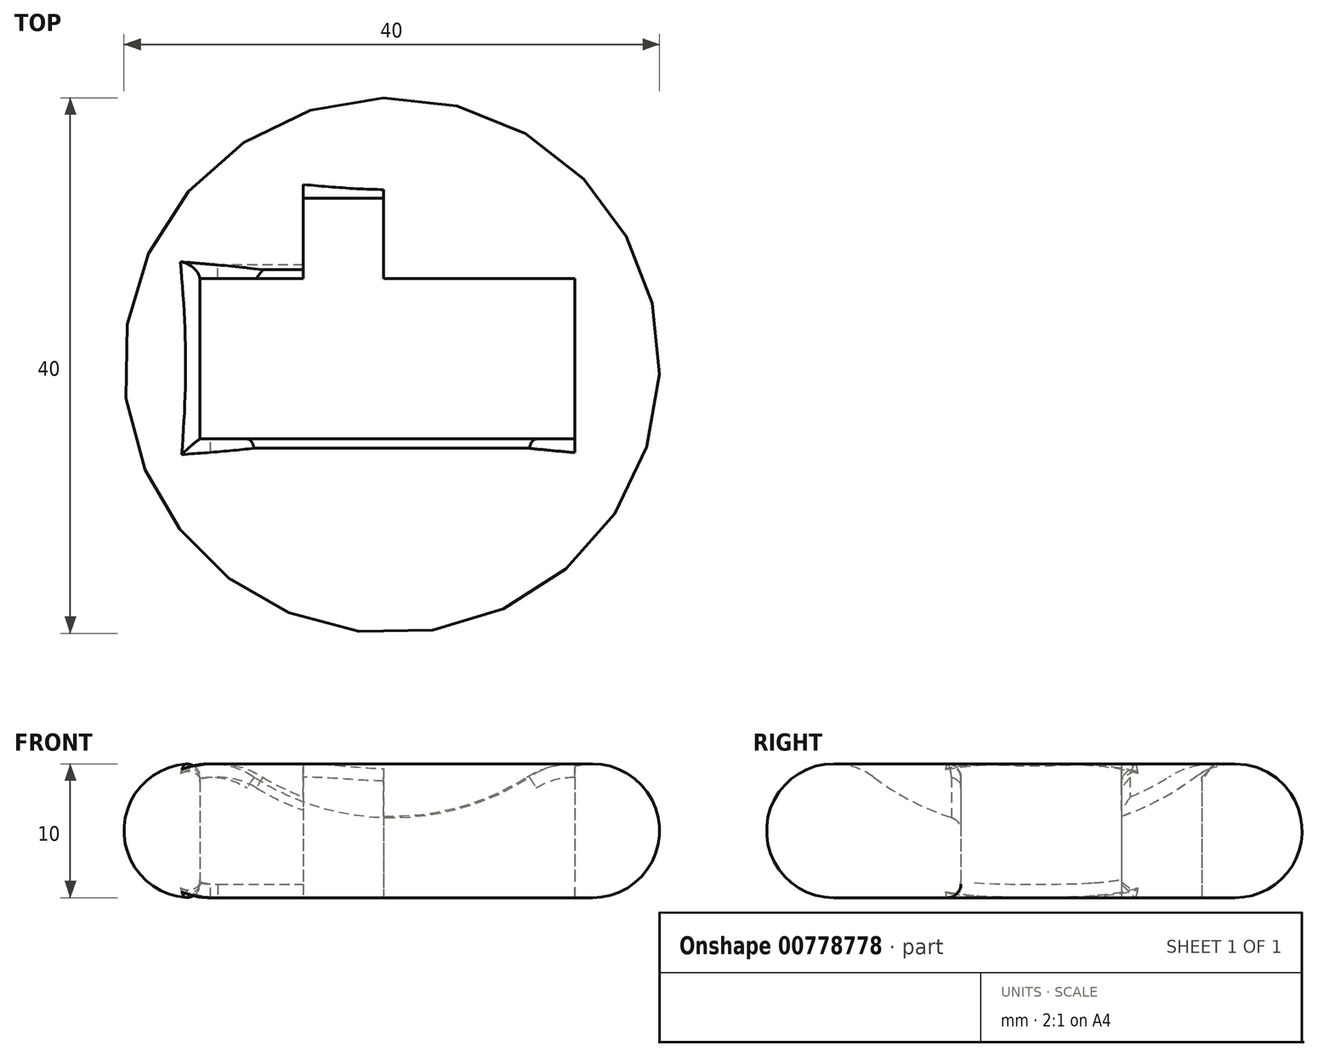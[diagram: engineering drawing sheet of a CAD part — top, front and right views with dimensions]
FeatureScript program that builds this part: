
annotation { "Feature Type Name" : "Feature", "Feature Type Description" : "" }
export const myFeature = defineFeature(function(context is Context, id is Id, definition is map)
    precondition{}
    {
        {
            var Q0;
            Q0=qCreatedBy(makeId("Front.planeOp"),FACE);
            var sketch = newSketch(context, id + "F0", { "sketchPlane" : qUnion([Q0])});
            skArc(sketch, "E0", {"start": v(-12, 9) * mm, "mid": v(-19.74, 6.58) * mm, "end": v(-15, 0) * mm});
            skArc(sketch, "E1", {"start": v(-12, 9) * mm, "mid": v(-6.32, 6.03) * mm, "end": v(0, 5) * mm});
            skLineSegment(sketch, "E2", {"start": v(0, 0) * mm, "end": v(-15, 0) * mm});
            skLineSegment(sketch, "E3", {"start": v(0, 0) * mm, "end": v(0, 5) * mm});
            skSolve(sketch);
        }
        {
            var Q0;
            Q0=makeQuery(id+"F0.imprint","IMPRINT",FACE,{"disambiguationData":[TD([[makeQuery(id+"F0.imprint","IMPRINT",EDGE,{"derivedFrom":sQuery(id+"F0.wireOp",EDGE,"E0")}),1.0]])]});
            var Q1;
            Q1=sQuery(id+"F0.wireOp",EDGE,"E3");
            revolve(context, id + "F1", {"surfaceOperationType" : NewSurfaceOperationType.NEW, "entities" : qUnion([Q0]), "axis" : qUnion([Q1]), "revolveType" : RevolveType.FULL});
        }
        {
            var Q0;
            Q0=qCreatedBy(makeId("Top.planeOp"),FACE);
            var sketch = newSketch(context, id + "F2", { "sketchPlane" : qUnion([Q0])});
            skLineSegment(sketch, "E4.bottom", {"start": v(-14.31, 6.51) * mm, "end": v(13.69, 6.51) * mm});
            skLineSegment(sketch, "E4.top", {"start": v(-14.31, -5.49) * mm, "end": v(13.69, -5.49) * mm});
            skLineSegment(sketch, "E4.left", {"start": v(-14.31, 6.51) * mm, "end": v(-14.31, -5.49) * mm});
            skLineSegment(sketch, "E4.right", {"start": v(13.69, 6.51) * mm, "end": v(13.69, -5.49) * mm});
            skLineSegment(sketch, "E5.bottom", {"start": v(-0.6, 12.51) * mm, "end": v(-6.6, 12.51) * mm});
            skLineSegment(sketch, "E5.top", {"start": v(-0.6, 6.51) * mm, "end": v(-6.6, 6.51) * mm});
            skLineSegment(sketch, "E5.left", {"start": v(-0.6, 12.51) * mm, "end": v(-0.6, 6.51) * mm});
            skLineSegment(sketch, "E5.right", {"start": v(-6.6, 12.51) * mm, "end": v(-6.6, 6.51) * mm});
            skSolve(sketch);
        }
        {
            var Q0;
            Q0 = qSketchRegion(id + "F2", true);
            extrude(context, id + "F3", {"entities" : qUnion([Q0]), "operationType" : NewBodyOperationType.REMOVE, "oppositeDirection" : true, "depth" : -25 * mm, "offsetDistance" : 25 * mm});
        }
        {
            var Q0;
            Q0=makeQuery(id+"F3.boolean.opBoolean","INTERSECT",EDGE,{"disambiguationData":[OD(0.0)],"derivedFrom":[makeQuery(id+"F1.opRevolve","SWEPT_FACE",FACE,{"disambiguationData":[OSD([sQuery(id+"F0.wireOp",EDGE,"E0")])]}),makeQuery(id+"F3.opExtrude","SWEPT_FACE",FACE,{"disambiguationData":[OSD([sQuery(id+"F2.wireOp",EDGE,"E4.left")])]})]});
            fillet(context, id + "F4", {"entities" : qUnion([Q0]), "radius" : 1 * mm, "tangentPropagation" : true, "allowEdgeOverflow" : false});
        }
        {
            var Q0;
            Q0=makeQuery(id+"F3.boolean.opBoolean","INTERSECT",EDGE,{"disambiguationData":[OD(2.0)],"derivedFrom":[makeQuery(id+"F1.opRevolve","SWEPT_FACE",FACE,{"disambiguationData":[OSD([sQuery(id+"F0.wireOp",EDGE,"E0")])]}),makeQuery(id+"F3.opExtrude","SWEPT_FACE",FACE,{"disambiguationData":[OSD([sQuery(id+"F2.wireOp",EDGE,"E4.top")])]})]});
            fillet(context, id + "F5", {"entities" : qUnion([Q0]), "radius" : 1 * mm, "tangentPropagation" : true, "allowEdgeOverflow" : false});
        }
        {
            var Q0;
            Q0=makeQuery(id+"F3.boolean.opBoolean","COPY",EDGE,{"derivedFrom":makeQuery(id+"F3.opExtrude","CAP_EDGE",EDGE,{"disambiguationData":[OSD([sQuery(id+"F2.wireOp",EDGE,"E4.top")])],"isStart":true})});
            var Q1;
            {var subQ0=sQuery(id+"F2.wireOp",EDGE,"E4.bottom");Q1=makeQuery(id+"F3.boolean.opBoolean","INTERSECT",EDGE,{"disambiguationData":[OD(1.0)],"derivedFrom":[makeQuery(id+"F1.opRevolve","SWEPT_FACE",FACE,{"disambiguationData":[OSD([sQuery(id+"F0.wireOp",EDGE,"E0")])]}),makeQuery(id+"F3.opExtrude","SWEPT_FACE",FACE,{"disambiguationData":[OSD([subQ0]),TDD([makeQuery(id+"F2.imprint","IMPRINT",EDGE,{"disambiguationData":[TD([[makeQuery(id+"F2.imprint","INTERSECT",VERTEX,{"derivedFrom":[subQ0,sQuery(id+"F2.wireOp",EDGE,"E4.left")]}),-1.0]])],"derivedFrom":subQ0})])]})]});}
            var Q2;
            Q2=makeQuery(id+"F3.boolean.opBoolean","INTERSECT",EDGE,{"derivedFrom":[makeQuery(id+"F1.opRevolve","SWEPT_FACE",FACE,{"disambiguationData":[OSD([sQuery(id+"F0.wireOp",EDGE,"E0")])]}),makeQuery(id+"F3.opExtrude","SWEPT_FACE",FACE,{"disambiguationData":[OSD([sQuery(id+"F2.wireOp",EDGE,"E5.bottom")])]})]});
            chamfer(context, id + "F6", {"entities" : qUnion([Q0, Q1, Q2]), "width" : 1 * mm, "tangentPropagation" : true});
        }
    });
